# Revit family: GR_Адаптер линейный_Муфта(n)_VL-G-КСД-У_П_R21
name_source: partatom
category: Соединительные детали воздуховодов
units: mm (PartAtom-declared; Revit-internal decimal feet)

## family parameters
Всегда вертикально = Да
Заголовок OmniClass = Metal Ducts
На основе рабочей плоскости = Нет
Номер OmniClass = 23.75.70.14.31
Общий = Нет
При загрузке вырезать с полостями = Нет
Размер круглого соединителя = Использовать диаметр
Тип детали = Мультипорт

## types (15) — shared parameters
ADSK_URL страницы изделия = https://grilles.ru
ADSK_Версия Revit = 2021
ADSK_Единица измерения = шт.
ADSK_Завод-изготовитель = ООО "ВЕНТРЕШЕТКИКОМ"
ADSK_Код изделия = 000158
ADSK_Количество = 1
ADSK_Материал = ADSK_Оцинкованная сталь
ADSK_Наименование = VL-G-КСД-У-П, адаптер вентиляционной решётки радиальный
Изготовитель = ООО "ВЕНТРЕШЕТКИКОМ"
Корпус_Металл_Толщина = 1 мм
Муфта_Металл_Толщина = 1 мм
zero-valued in all types: Отметка по умолчанию

## per-type parameters (varying)
| type | Корпус_Высота | Корпус_Длина | Решетка_отступ | Решётка_Высота |
| VL-G-КСД-У-П 1-20 | 75 мм | 191 мм | 37 мм | 72 мм |
| VL-G-КСД-У-П 1-30 | 75 мм | 201 мм | 42 мм | 82 мм |
| VL-G-КСД-У-П 1-40 | 105 мм | 211 мм | 47 мм | 92 мм |
| VL-G-КСД-У-П 1-50 | 105 мм | 221 мм | 52 мм | 102 мм |
| VL-G-КСД-У-П 1-60 | 140 мм | 231 мм | 57 мм | 112 мм |
| VL-G-КСД-У-П 1-70 | 140 мм | 241 мм | 62 мм | 122 мм |
| VL-G-КСД-У-П 2-20 | 105 мм | 231 мм | 57 мм | 112 мм |
| VL-G-КСД-У-П 2-25 | 105 мм | 241 мм | 62 мм | 122 мм |
| VL-G-КСД-У-П 2-30 | 105 мм | 251 мм | 67 мм | 132 мм |
| VL-G-КСД-У-П 3-20 | 105 мм | 271 мм | 77 мм | 152 мм |
| VL-G-КСД-У-П 3-25 | 105 мм | 286 мм | 85 мм | 167 мм |
| VL-G-КСД-У-П 3-30 | 105 мм | 301 мм | 92 мм | 182 мм |
| VL-G-КСД-У-П 4-20 | 140 мм | 311 мм | 97 мм | 192 мм |
| VL-G-КСД-У-П 4-25 | 140 мм | 331 мм | 107 мм | 212 мм |
| VL-G-КСД-У-П 4-30 | 140 мм | 351 мм | 117 мм | 232 мм |

note: column(s) folded — value = type name in every type: ADSK_Марка
